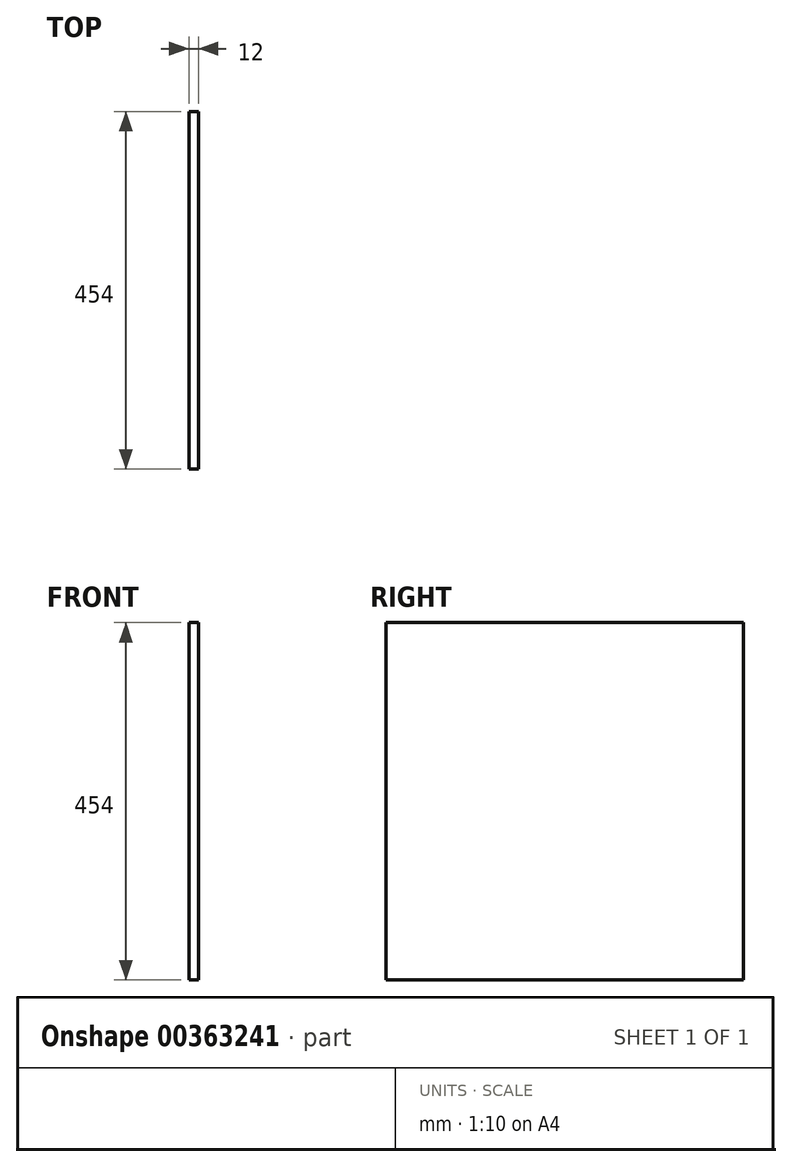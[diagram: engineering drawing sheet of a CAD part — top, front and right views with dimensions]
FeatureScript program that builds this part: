
annotation { "Feature Type Name" : "Feature", "Feature Type Description" : "" }
export const myFeature = defineFeature(function(context is Context, id is Id, definition is map)
    precondition{}
    {
        {
            assignVariable(context, id + "F0", {"name" : "thickness", "anyValue" : 12});
        }
        {
            var Q0;
            Q0=qCreatedBy(makeId("Right.planeOp"),FACE);
            var sketch = newSketch(context, id + "F1", { "sketchPlane" : qUnion([Q0])});
            skLineSegment(sketch, "E0.bottom", {"start": v(-227, 227) * mm, "end": v(227, 227) * mm});
            skLineSegment(sketch, "E0.top", {"start": v(-227, -227) * mm, "end": v(227, -227) * mm});
            skLineSegment(sketch, "E0.left", {"start": v(-227, 227) * mm, "end": v(-227, -227) * mm});
            skLineSegment(sketch, "E0.right", {"start": v(227, 227) * mm, "end": v(227, -227) * mm});
            skPoint(sketch, "E0.middle", {"position": v(0, 0) * mm});
            skSolve(sketch);
        }
        {
            var Q0;
            Q0=makeQuery(id+"F1.imprint","IMPRINT",FACE,{"disambiguationData":[TD([[makeQuery(id+"F1.imprint","IMPRINT",EDGE,{"derivedFrom":sQuery(id+"F1.wireOp",EDGE,"E0.bottom")}),-1.0]])]});
            extrude(context, id + "F2", {"entities" : qUnion([Q0]), "depth" : (getVariable(context, 'thickness')) * mm});
        }
    });
